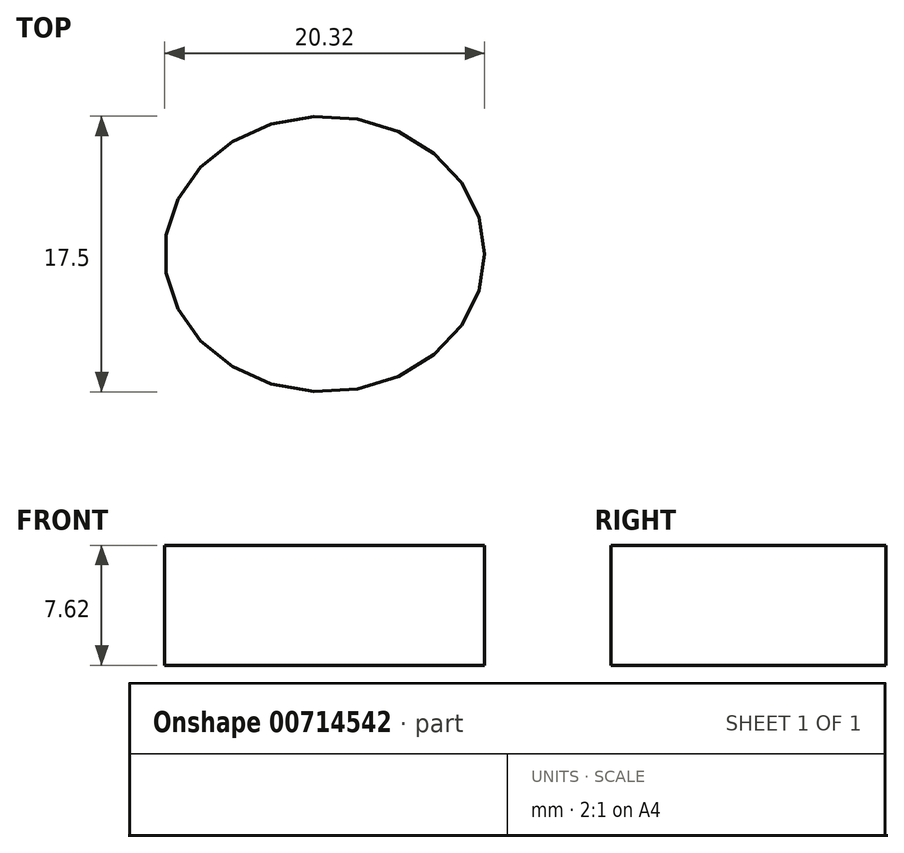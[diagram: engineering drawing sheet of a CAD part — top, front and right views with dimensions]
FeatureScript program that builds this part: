
annotation { "Feature Type Name" : "Feature", "Feature Type Description" : "" }
export const myFeature = defineFeature(function(context is Context, id is Id, definition is map)
    precondition{}
    {
        {
            var Q0;
            Q0=qCreatedBy(makeId("Top.planeOp"),FACE);
            var sketch = newSketch(context, id + "F0", { "sketchPlane" : qUnion([Q0])});
            skEllipse(sketch, "E0", {"center": v(0, 0) * mm, "majorRadius": 10.16 * mm, "minorRadius": 8.75 * mm, "majorAxis": v(1, 0)});
            skSolve(sketch);
        }
        {
            var Q0;
            Q0=sQuery(id+"F0.wireOp",EDGE,"E0");
            extrude(context, id + "F1", {"bodyType" : ToolBodyType.SURFACE, "surfaceEntities" : qUnion([Q0]), "endBound" : BoundingType.SYMMETRIC, "depth" : 7.62 * mm, "offsetDistance" : 25.4 * mm, "hasDraft" : true, "draftAngle" : 3 * degree});
        }
    });
